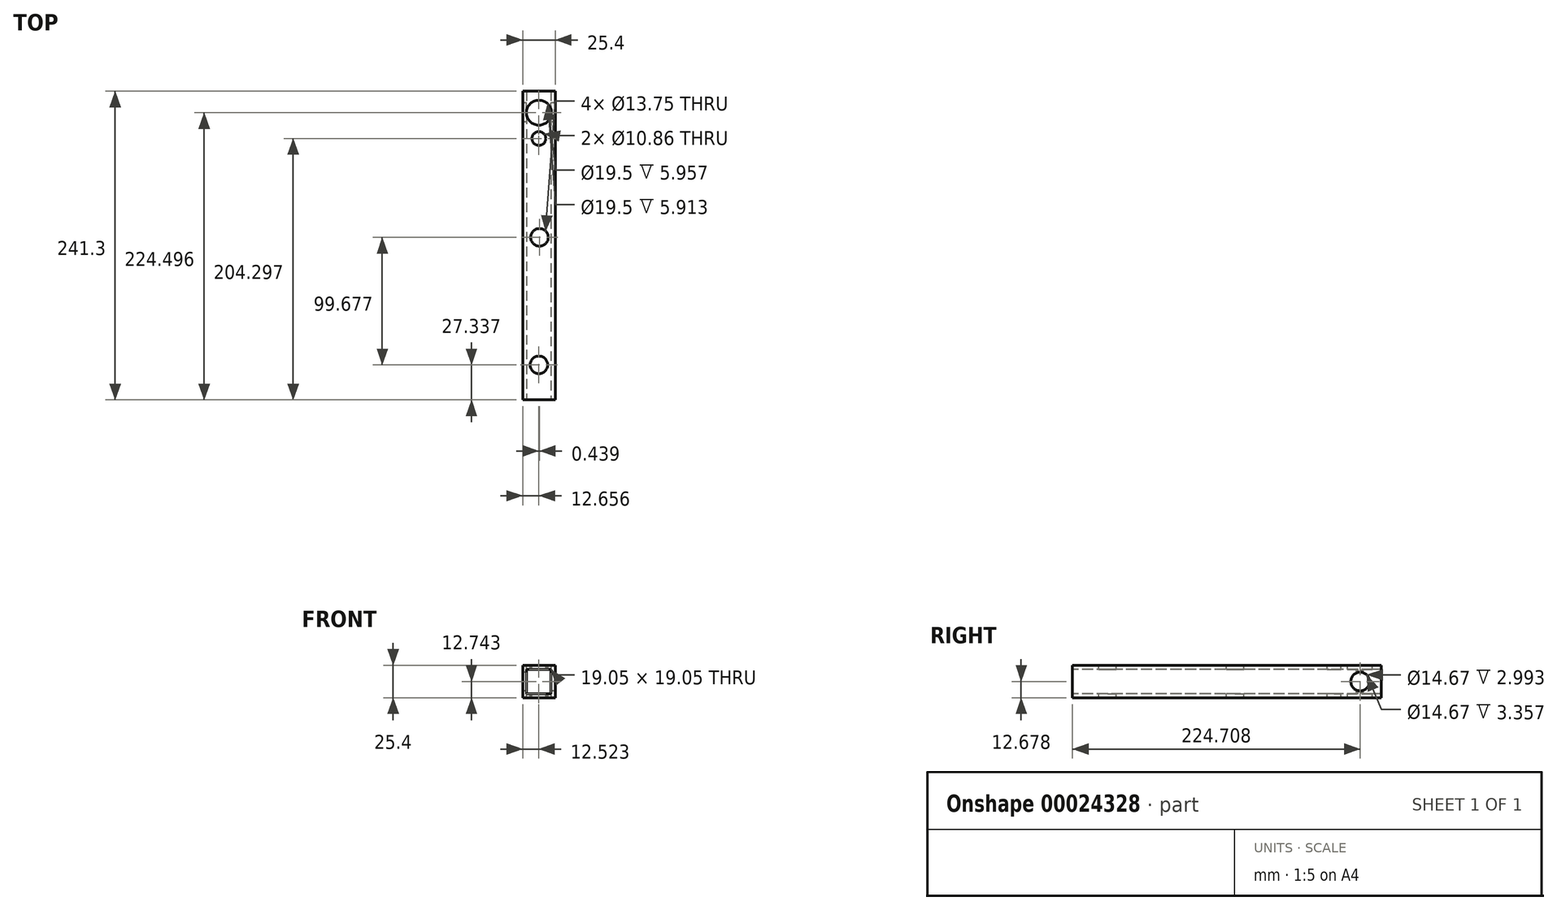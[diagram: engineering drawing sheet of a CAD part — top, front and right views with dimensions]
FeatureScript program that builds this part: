
annotation { "Feature Type Name" : "Feature", "Feature Type Description" : "" }
export const myFeature = defineFeature(function(context is Context, id is Id, definition is map)
    precondition{}
    {
        {
            var Q0;
            Q0=qCreatedBy(makeId("Top.planeOp"),FACE);
            var sketch = newSketch(context, id + "F0", { "sketchPlane" : qUnion([Q0])});
            skLineSegment(sketch, "E0", {"start": v(-60.08, 121.67) * mm, "end": v(-60.08, -119.63) * mm});
            skLineSegment(sketch, "E1", {"start": v(-60.08, -119.63) * mm, "end": v(-34.68, -119.63) * mm});
            skLineSegment(sketch, "E2", {"start": v(-34.68, -119.63) * mm, "end": v(-34.68, 121.67) * mm});
            skLineSegment(sketch, "E3", {"start": v(-34.68, 121.67) * mm, "end": v(-60.08, 121.67) * mm});
            skSolve(sketch);
        }
        {
            var Q0;
            Q0=makeQuery(id+"F0.imprint","IMPRINT",FACE,{"disambiguationData":[TD([[makeQuery(id+"F0.imprint","IMPRINT",EDGE,{"derivedFrom":sQuery(id+"F0.wireOp",EDGE,"E0")}),1.0]])]});
            extrude(context, id + "F1", {"entities" : qUnion([Q0]), "depth" : 25.4 * mm});
        }
        {
            var Q0;
            Q0=makeQuery(id+"F1.opExtrude","SWEPT_FACE",FACE,{"disambiguationData":[OSD([sQuery(id+"F0.wireOp",EDGE,"E1")])]});
            var sketch = newSketch(context, id + "F2", { "sketchPlane" : qUnion([Q0])});
            skLineSegment(sketch, "E4", {"start": v(-57.08, 22.27) * mm, "end": v(-57.08, 3.22) * mm});
            skLineSegment(sketch, "E5", {"start": v(-57.08, 3.22) * mm, "end": v(-38.03, 3.22) * mm});
            skLineSegment(sketch, "E6", {"start": v(-38.03, 3.22) * mm, "end": v(-38.03, 22.27) * mm});
            skLineSegment(sketch, "E7", {"start": v(-38.03, 22.27) * mm, "end": v(-57.08, 22.27) * mm});
            skSolve(sketch);
        }
        {
            var Q0;
            Q0 = qSketchRegion(id + "F2", true);
            extrude(context, id + "F3", {"entities" : qUnion([Q0]), "operationType" : NewBodyOperationType.REMOVE, "oppositeDirection" : true, "depth" : 277.64 * mm});
        }
        {
            var Q0;
            Q0=makeQuery(id+"F1.opExtrude","CAP_FACE",FACE,{"disambiguationData":[OSD([sQuery(id+"F0.wireOp",EDGE,"E0"),sQuery(id+"F0.wireOp",EDGE,"E1"),sQuery(id+"F0.wireOp",EDGE,"E2"),sQuery(id+"F0.wireOp",EDGE,"E3")])],"isStart":false});
            var sketch = newSketch(context, id + "F4", { "sketchPlane" : qUnion([Q0])});
            skCircle(sketch, "E8", {"center": v(-47.42, 104.87) * mm, "radius": 9.75 * mm});
            skCircle(sketch, "E9", {"center": v(-47.42, 84.67) * mm, "radius": 5.43 * mm});
            skCircle(sketch, "E10", {"center": v(-46.98, 7.38) * mm, "radius": 6.87 * mm});
            skCircle(sketch, "E11", {"center": v(-47.42, -92.3) * mm, "radius": 6.87 * mm});
            skSolve(sketch);
        }
        {
            var Q0;
            Q0 = qSketchRegion(id + "F4", true);
            extrude(context, id + "F5", {"entities" : qUnion([Q0]), "operationType" : NewBodyOperationType.REMOVE, "oppositeDirection" : true, "depth" : 72.47 * mm});
        }
        {
            var Q0;
            Q0=makeQuery(id+"F1.opExtrude","SWEPT_FACE",FACE,{"disambiguationData":[OSD([sQuery(id+"F0.wireOp",EDGE,"E0")])]});
            var sketch = newSketch(context, id + "F6", { "sketchPlane" : qUnion([Q0])});
            skCircle(sketch, "E12", {"center": v(-105.08, 12.68) * mm, "radius": 7.33 * mm});
            skSolve(sketch);
        }
        {
            var Q0;
            Q0 = qSketchRegion(id + "F6", true);
            extrude(context, id + "F7", {"entities" : qUnion([Q0]), "operationType" : NewBodyOperationType.REMOVE, "oppositeDirection" : true, "depth" : 90.9 * mm});
        }
    });
